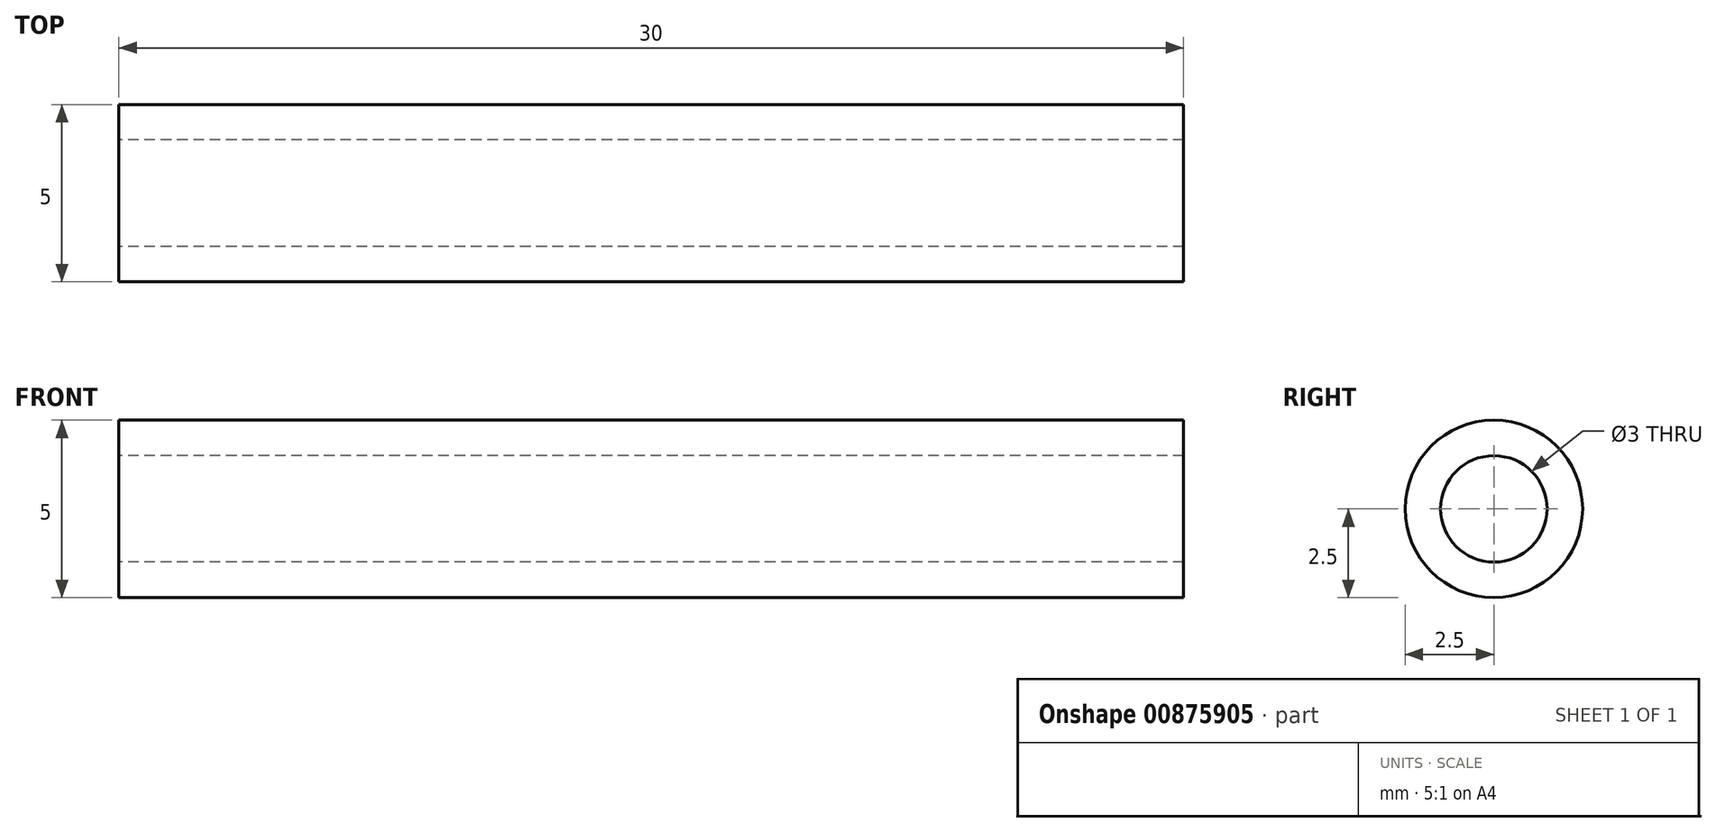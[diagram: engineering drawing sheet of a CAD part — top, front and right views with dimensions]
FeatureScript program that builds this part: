
annotation { "Feature Type Name" : "Feature", "Feature Type Description" : "" }
export const myFeature = defineFeature(function(context is Context, id is Id, definition is map)
    precondition{}
    {
        {
            var Q0;
            Q0=qCreatedBy(makeId("Right.planeOp"),FACE);
            var sketch = newSketch(context, id + "F0", { "sketchPlane" : qUnion([Q0])});
            skCircle(sketch, "E0", {"center": v(0, 0) * mm, "radius": 2.5 * mm});
            skCircle(sketch, "E1", {"center": v(0, 0) * mm, "radius": 1.5 * mm});
            skSolve(sketch);
        }
        {
            var Q0;
            Q0 = qSketchRegion(id + "F0", true);
            extrude(context, id + "F1", {"entities" : qUnion([Q0]), "endBound" : BoundingType.SYMMETRIC, "depth" : 30 * mm, "offsetDistance" : 25 * mm});
        }
    });
